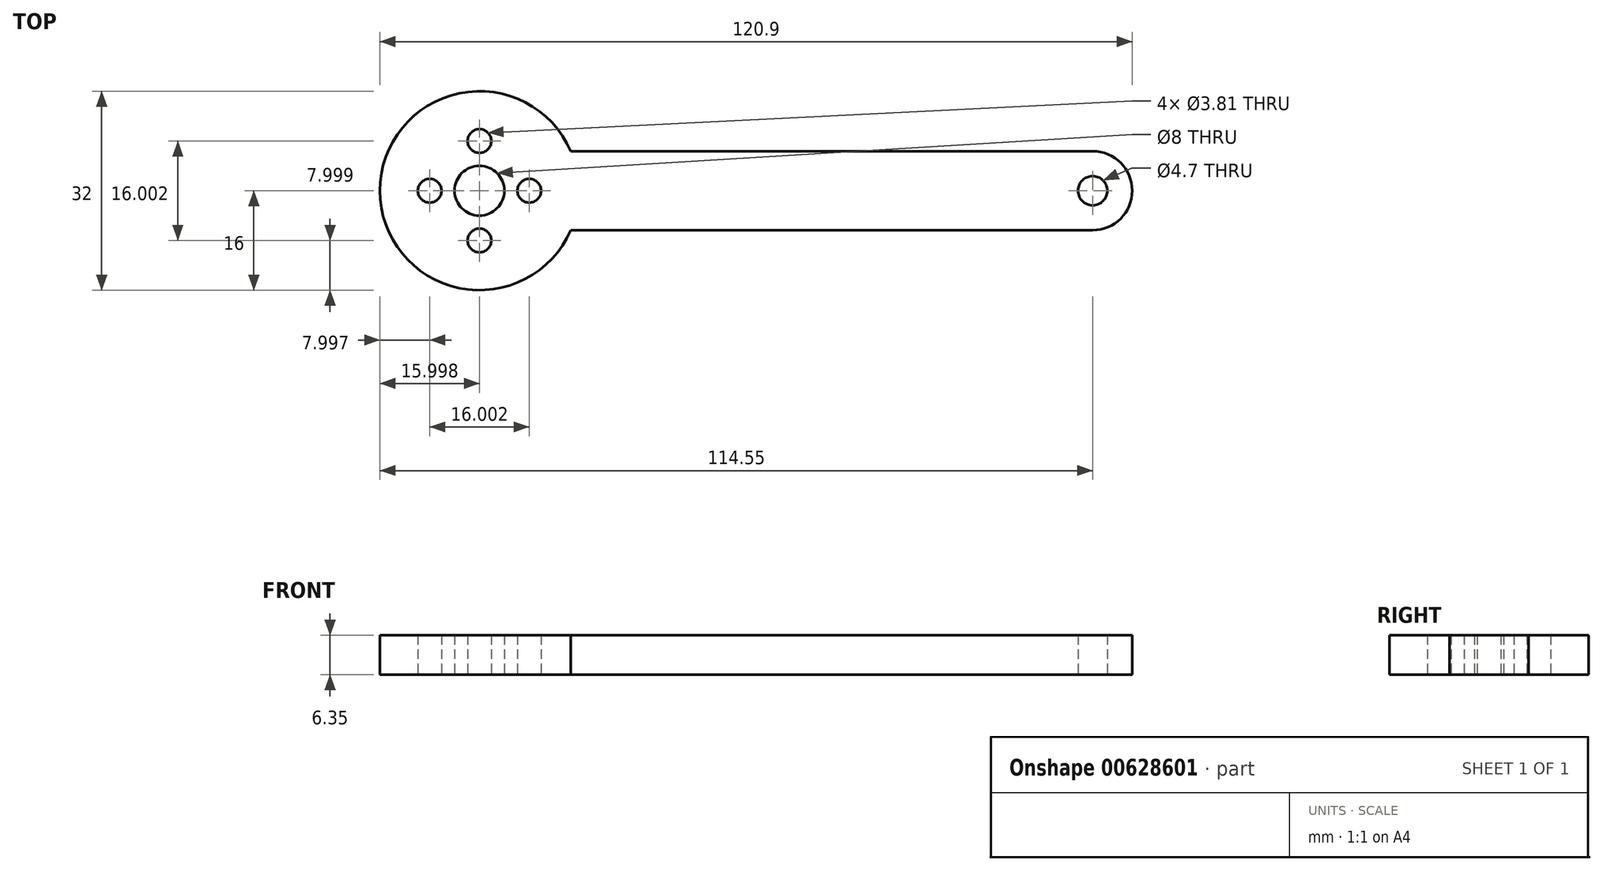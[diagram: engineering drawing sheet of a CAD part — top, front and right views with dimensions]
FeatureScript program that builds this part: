
annotation { "Feature Type Name" : "Feature", "Feature Type Description" : "" }
export const myFeature = defineFeature(function(context is Context, id is Id, definition is map)
    precondition{}
    {
        {
            var Q0;
            Q0=qCreatedBy(makeId("Top.planeOp"),FACE);
            var sketch = newSketch(context, id + "F0", { "sketchPlane" : qUnion([Q0])});
            skLineSegment(sketch, "E0", {"start": v(0, 6.35) * mm, "end": v(0, 6.35) * mm});
            skLineSegment(sketch, "E1", {"start": v(-6.35, 12.7) * mm, "end": v(-88.9, 12.7) * mm});
            skLineSegment(sketch, "E2", {"start": v(-88.9, 0) * mm, "end": v(-6.35, 0) * mm});
            skArc(sketch, "E3", {"start": v(-90.22, 12.7) * mm, "mid": v(-120.9, 6.35) * mm, "end": v(-90.22, 0) * mm});
            skLineSegment(sketch, "E4", {"start": v(-88.9, 12.7) * mm, "end": v(-90.22, 12.7) * mm});
            skLineSegment(sketch, "E5", {"start": v(-88.9, 0) * mm, "end": v(-90.22, 0) * mm});
            skPoint(sketch, "E6.start.orphan", {"position": v(-88.9, 6.35) * mm});
            skCircle(sketch, "E7", {"center": v(-104.9, 6.35) * mm, "radius": 4 * mm});
            skCircle(sketch, "E8", {"center": v(-104.9, 14.35) * mm, "radius": 1.9 * mm});
            skCircle(sketch, "E9.1.0", {"center": v(-112.9, 6.35) * mm, "radius": 1.9 * mm});
            skCircle(sketch, "E9.2.0", {"center": v(-104.9, -1.65) * mm, "radius": 1.9 * mm});
            skCircle(sketch, "E9.3.0", {"center": v(-96.9, 6.35) * mm, "radius": 1.9 * mm});
            skPoint(sketch, "E10.visualSharp", {"position": v(0, 12.7) * mm});
            skArc(sketch, "E10.filletArc", {"start": v(0, 6.35) * mm, "mid": v(-1.86, 10.84) * mm, "end": v(-6.35, 12.7) * mm});
            skPoint(sketch, "E11.visualSharp", {"position": v(0, 0) * mm});
            skArc(sketch, "E11.filletArc", {"start": v(-6.35, 0) * mm, "mid": v(-1.86, 1.86) * mm, "end": v(0, 6.35) * mm});
            skCircle(sketch, "E12", {"center": v(-6.35, 6.35) * mm, "radius": 2.35 * mm});
            skSolve(sketch);
        }
        {
            var Q0;
            Q0=makeQuery(id+"F0.imprint","IMPRINT",FACE,{"disambiguationData":[TD([[makeQuery(id+"F0.imprint","IMPRINT",EDGE,{"derivedFrom":sQuery(id+"F0.wireOp",EDGE,"E1")}),1.0]])]});
            extrude(context, id + "F1", {"entities" : qUnion([Q0]), "depth" : 6.35 * mm, "offsetDistance" : 25.4 * mm});
        }
    });
